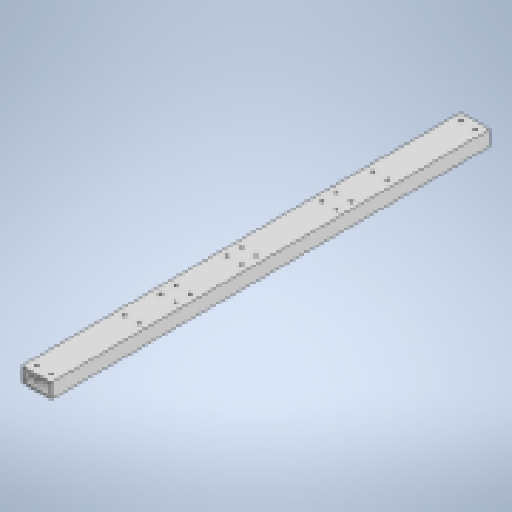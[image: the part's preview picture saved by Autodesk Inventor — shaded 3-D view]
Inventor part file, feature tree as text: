
AUTODESK INVENTOR PART (.ipt)
format: ipt  version: 2023 (Build 270158000, 158)  size: 250,368 bytes
history: native  units: in
note: dims shown in document units (in); Inventor stores cm internally (conversion verified against a paired STEP export)
features: sketch x17, hole x16, extrude x1
ambient origin geometry x8: Origin, YZ Plane, XZ Plane, XY Plane, X Axis, Y Axis, Z Axis, Center Point
bodies: Solid1 (feature_tree)
feature tree (34):
  extrude  "Extrusion1"  Depth=1.0in
  hole  "Hole1"  [1 undecoded]
  hole  "Hole2"  [1 undecoded]
  hole  "Hole3"  [1 undecoded]
  hole  "Hole4"  [1 undecoded]
  hole  "Hole5"  [1 undecoded]
  hole  "Hole6"  [1 undecoded]
  hole  "Hole7"  [1 undecoded]
  hole  "Hole8"  [1 undecoded]
  hole  "Hole13"  [1 undecoded]
  hole  "Hole14"  [1 undecoded]
  hole  "Hole15"  [1 undecoded]
  hole  "Hole16"  [1 undecoded]
  hole  "Hole17"  [1 undecoded]
  hole  "Hole18"  [1 undecoded]
  hole  "Hole19"  [1 undecoded]
  hole  "Hole20"  [1 undecoded]
  sketch  "Sketch1"  dims[d0=2.0in d1=1.0in]
  sketch  "Sketch2"  dims[d2=0.125in d3=0.125in]
  sketch  "Sketch3"  dims[d4=0.125in d5=0.125in]
  sketch  "Sketch4"  dims[d6=30.0in d7=0.0in d8=0.5in]
  sketch  "Sketch5"  dims[d9=0.5in]
  sketch  "Sketch6"  dims[d10=0.1875in d11=0.75in d12=0.375in d13=0.25in d14=0.5635in d15=1.1in d16=0.0in d17=0.5in]
  sketch  "Sketch7"  dims[d18=0.5in]
  sketch  "Sketch8"  dims[d19=0.1875in d20=0.75in d21=0.375in d22=0.25in d23=0.5635in d24=1.1in d25=0.0in d26=0.5in]
  sketch  "Sketch9"  dims[d27=6.5in]
  sketch  "Sketch14"  dims[d28=0.1875in d29=0.75in d30=0.375in d31=0.25in d32=0.5635in d33=1.1in d34=0.0in d35=0.5in]
  sketch  "Sketch15"  dims[d36=6.5in]
  sketch  "Sketch16"  dims[d37=0.1875in d38=0.75in d39=0.375in d40=0.25in d41=0.5635in d42=1.1in d43=0.0in d44=0.5in]
  sketch  "Sketch17"  dims[d45=0.5in]
  sketch  "Sketch18"  dims[d46=0.1875in d47=0.75in d48=0.375in d49=0.25in d50=0.5635in d51=1.1in d52=0.0in d53=0.5in]
  sketch  "Sketch19"  dims[d54=0.5in]
  sketch  "Sketch20"  dims[d55=0.1875in d56=0.75in d57=0.375in d58=0.25in d59=0.5635in d60=1.1in d61=0.0in d62=6.5in]
  sketch  "Sketch21"  dims[d63=0.5in d64=0.1875in d65=0.75in d66=0.375in d67=0.25in d68=0.5635in d69=1.1in d70=0.0in d71=6.5in d72=0.5in d73=0.1875in d74=0.75in d75=0.375in d76=0.25in d77=0.5635in d78=1.1in d79=0.0in d116=0.5in d117=10.0in d118=0.1875in d119=0.75in d120=0.375in d121=0.25in d122=0.5635in d123=4.1in d124=0.0in d125=1.5in d126=10.0in d127=0.1875in d128=0.75in d129=0.375in d130=0.25in d131=0.5635in d132=4.1in d133=0.0in d134=0.5in d135=9.0in d136=0.1875in d137=0.75in d138=0.375in d139=0.25in d140=0.5635in d141=4.1in d142=0.0in d143=9.0in d144=0.5in d145=0.1875in d146=0.75in d147=0.375in d148=0.25in d149=0.5635in d150=4.1in d151=0.0in d152=0.5in d153=13.5in d154=0.1875in d155=0.75in d156=0.375in d157=0.25in d158=0.5635in d159=4.1in d160=0.0in d161=0.5in d162=13.5in d163=0.1875in d164=0.75in d165=0.375in d166=0.25in d167=0.5635in d168=4.1in d169=0.0in d170=0.5in d171=15.5in d172=0.1875in d173=0.75in d174=0.375in d175=0.25in d176=0.5635in d177=4.1in d178=0.0in d179=1.5in d180=15.5in d181=0.1875in d182=0.75in d183=0.375in d184=0.25in d185=0.5635in d186=4.1in d187=0.0in]
note: 16 required parameter values undecoded (feature->parameter linkage not recoverable at this tier; creation-order binding heuristic only, values carry confidence <= 0.55)
